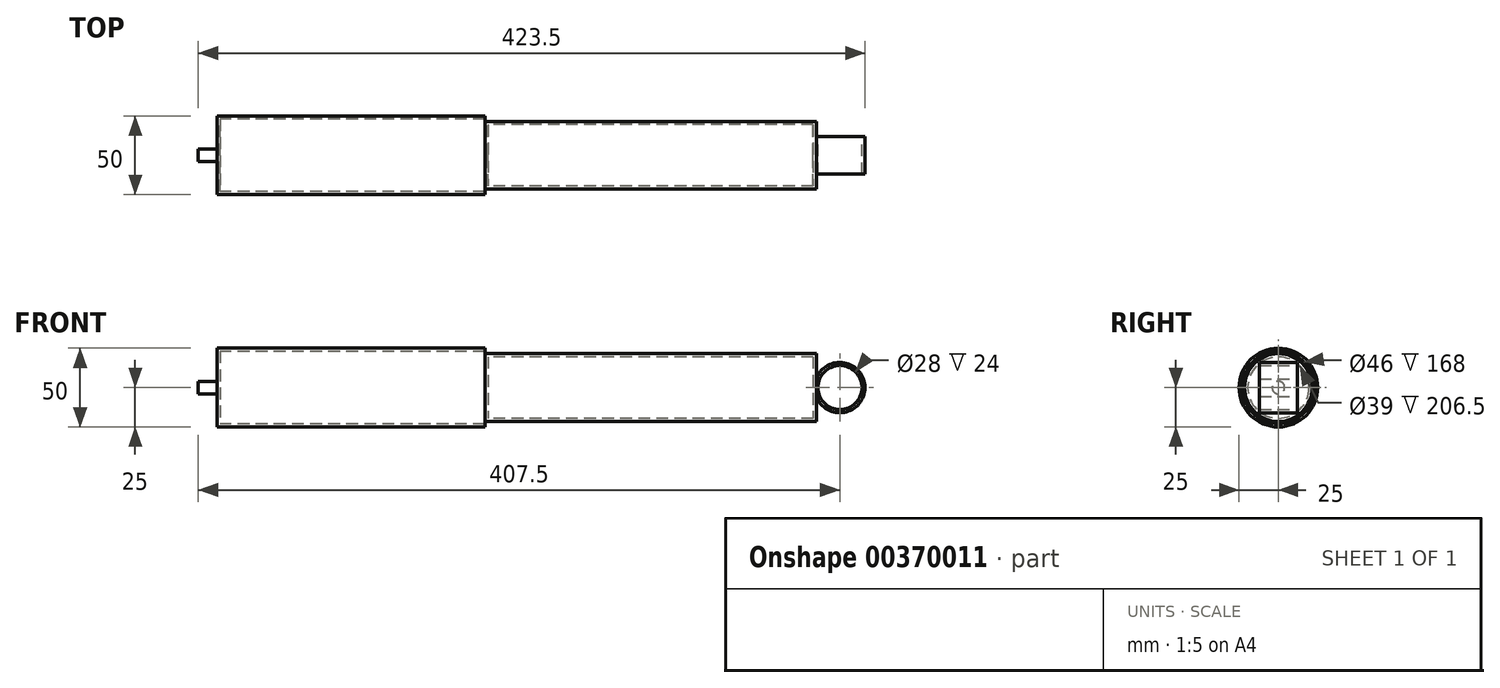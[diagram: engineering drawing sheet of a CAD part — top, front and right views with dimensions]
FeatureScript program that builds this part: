
annotation { "Feature Type Name" : "Feature", "Feature Type Description" : "" }
export const myFeature = defineFeature(function(context is Context, id is Id, definition is map)
    precondition{}
    {
        {
            var Q0;
            Q0=qCreatedBy(makeId("Front.planeOp"),FACE);
            var sketch = newSketch(context, id + "F0", { "sketchPlane" : qUnion([Q0])});
            skLineSegment(sketch, "E0", {"start": v(0, 0) * mm, "end": v(500, 0) * mm, "construction": true});
            skLineSegment(sketch, "E1", {"start": v(0, 0) * mm, "end": v(0, 4) * mm});
            skLineSegment(sketch, "E2", {"start": v(0, 4) * mm, "end": v(12, 4) * mm});
            skLineSegment(sketch, "E3", {"start": v(12, 4) * mm, "end": v(12, 0) * mm});
            skLineSegment(sketch, "E4", {"start": v(12, 0) * mm, "end": v(12, 25) * mm});
            skLineSegment(sketch, "E5", {"start": v(12, 25) * mm, "end": v(182, 25) * mm});
            skLineSegment(sketch, "E6", {"start": v(182, 25) * mm, "end": v(182, 0) * mm});
            skLineSegment(sketch, "E7", {"start": v(182, 23) * mm, "end": v(12, 23) * mm});
            skLineSegment(sketch, "E8", {"start": v(0, 0) * mm, "end": v(12, 0) * mm});
            skLineSegment(sketch, "E9", {"start": v(14, 0) * mm, "end": v(14, 23) * mm});
            skLineSegment(sketch, "E10", {"start": v(12, 0) * mm, "end": v(14, 0) * mm});
            skLineSegment(sketch, "E11", {"start": v(182, 0) * mm, "end": v(182, 21.5) * mm});
            skLineSegment(sketch, "E12", {"start": v(182, 21.5) * mm, "end": v(392.5, 21.5) * mm});
            skLineSegment(sketch, "E13", {"start": v(392.5, 21.5) * mm, "end": v(392.5, 0) * mm});
            skLineSegment(sketch, "E14", {"start": v(392.5, 19.5) * mm, "end": v(182, 19.5) * mm});
            skLineSegment(sketch, "E15", {"start": v(182, 0) * mm, "end": v(184, 0) * mm});
            skLineSegment(sketch, "E16", {"start": v(184, 0) * mm, "end": v(184, 19.5) * mm});
            skLineSegment(sketch, "E17", {"start": v(184, 7) * mm, "end": v(182, 7) * mm});
            skLineSegment(sketch, "E18", {"start": v(390.5, 0) * mm, "end": v(390.5, 19.5) * mm});
            skLineSegment(sketch, "E19", {"start": v(390.5, 0) * mm, "end": v(392.5, 0) * mm});
            skSolve(sketch);
        }
        {
            var Q0;
            Q0 = qSketchRegion(id + "F0", true);
            var Q1;
            Q1=sQuery(id+"F0.wireOp",EDGE,"E0");
            revolve(context, id + "F1", {"entities" : qUnion([Q0]), "axis" : qUnion([Q1]), "revolveType" : RevolveType.FULL});
        }
        {
            var Q0;
            Q0=qCreatedBy(makeId("Front.planeOp"),FACE);
            var sketch = newSketch(context, id + "F2", { "sketchPlane" : qUnion([Q0])});
            skPoint(sketch, "E20", {"position": v(407.5, 0) * mm});
            skCircle(sketch, "E21", {"center": v(407.5, 0) * mm, "radius": 16 * mm});
            skCircle(sketch, "E22", {"center": v(407.5, 0) * mm, "radius": 14 * mm});
            skSolve(sketch);
        }
        {
            var Q0;
            Q0 = qSketchRegion(id + "F2", true);
            extrude(context, id + "F3", {"entities" : qUnion([Q0]), "operationType" : NewBodyOperationType.ADD, "endBound" : BoundingType.SYMMETRIC, "depth" : 24 * mm});
        }
    });
